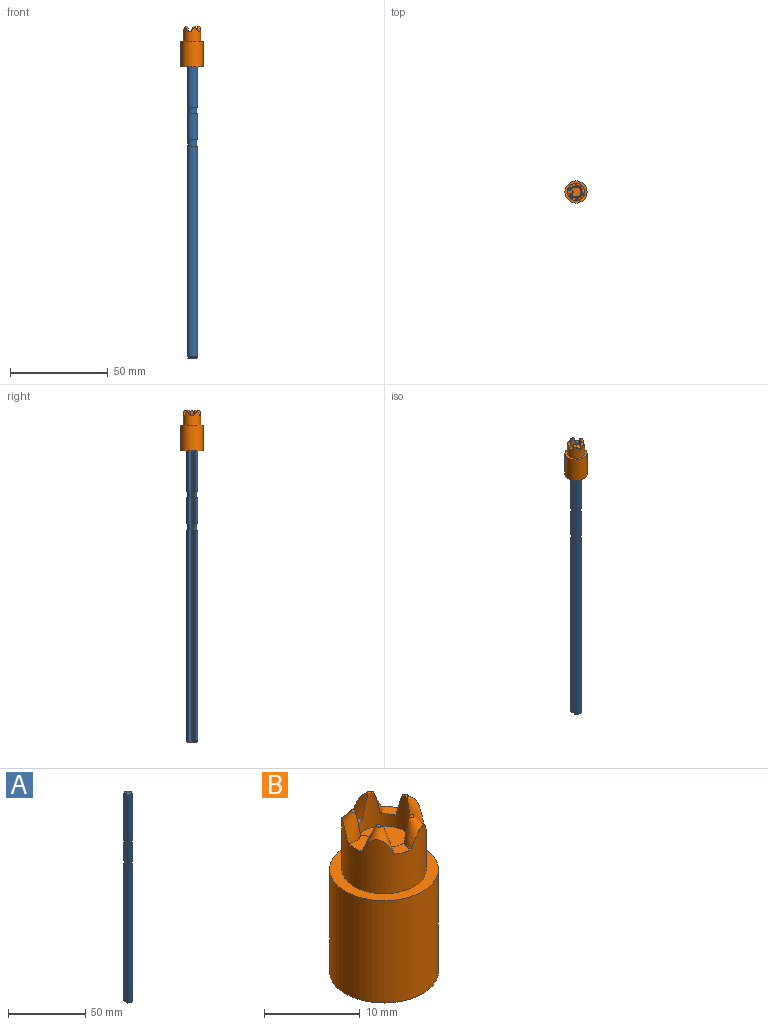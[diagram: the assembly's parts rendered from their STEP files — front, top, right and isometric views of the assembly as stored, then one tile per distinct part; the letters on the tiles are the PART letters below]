
ASSEMBLY  parts=2 mates=1
PART A: 16 faces, bbox 5.6x5.9x165 mm
  f0: cylinder r=2.95mm len=13.2mm, axis (0,0,-1), area 201.2mm2, adj f2,f4,f11,f15
  f1: cylinder r=2.95mm len=107.85mm, axis (0,0,-1), area 1643.7mm2, adj f2,f4,f8,f12
  f2: plane 165.02x1.36mm, normal (-0.71,0.71,0), area 307.8mm2, adj f0,f1,f3,f5,f6,f7,f8,f9
  f3: cylinder r=2.95mm len=35.25mm, axis (0,0,-1), area 537.2mm2, adj f2,f4,f9,f14
  f4: plane 165.02x1.36mm, normal (-0.71,-0.71,0), area 307.8mm2, adj f0,f1,f3,f5,f6,f7,f8,f9
  f5: cylinder r=0.3mm len=165mm, axis (0,0,-1), area 77.8mm2, adj f2,f4,f6,f7
  f6: plane 5.09x4.75mm, normal (0,0,1), area 18.2mm2, adj f2,f4,f5,f9
  f7: plane 4.69x4.41mm, normal (0,0,-1), area 15.6mm2, adj f2,f4,f5,f8
  f8: cone r=2.95mm half-angle=45deg, axis (0,0,1), area 11.7mm2, adj f1,f2,f4,f7
  f9: cone r=2.54mm half-angle=15deg, axis (0,0,-1), area 22.2mm2, adj f2,f3,f4,f6
  f10: cylinder r=2.4mm len=4.8mm, axis (0,0,-1), area 41.8mm2, adj f2,f4,f11,f12
  f11: plane 5.89x5.45mm, normal (0,0,-1), area 7.6mm2, adj f0,f2,f4,f10
  f12: plane 5.89x5.45mm, normal (0,0,1), area 7.6mm2, adj f1,f2,f4,f10
  f13: cylinder r=2.4mm len=4.8mm, axis (0,0,-1), area 41.8mm2, adj f2,f4,f14,f15
  f14: plane 5.89x5.45mm, normal (0,0,-1), area 7.6mm2, adj f2,f3,f4,f13
  f15: plane 5.89x5.45mm, normal (0,0,1), area 7.6mm2, adj f0,f2,f4,f13
PART B: 33 faces, bbox 11.7x11.7x21.3 mm
  f0: cylinder r=3.06mm len=6.12mm, axis (0,0,-1), area 44.5mm2, adj f1,f4,f6,f7,f10,f11,f12,f13
  f1: cylinder r=0.15mm len=4.37mm, axis (0,0,-1), area 0.8mm2, adj f0,f2,f17,f32
  f2: plane 3.77x0.68mm, normal (0.71,0.71,0), area 1.9mm2, adj f1,f5,f17,f18,f32
  f3: plane 3.77x0.68mm, normal (0.71,-0.71,0), area 1.9mm2, adj f4,f5,f18,f22,f32
  f4: cylinder r=0.15mm len=4.37mm, axis (0,0,-1), area 0.8mm2, adj f0,f3,f22,f32
  f5: cylinder r=0.9mm len=1.57mm, axis (0,0,-1), area 2.2mm2, adj f2,f3,f18,f32
  f6: cone r=1.8mm half-angle=24.8deg, axis (0.34,0,-0.94), area 9mm2, adj f0,f7,f9,f10,f27
  f7: plane 0.97x0.71mm, normal (0,0,1), area 0.2mm2, adj f0,f6
  f8: cylinder r=3.06mm len=15.9mm, axis (0,0,-1), area 255.9mm2, adj f15,f21,f29,f31
  f9: cylinder r=4.4mm len=8.8mm, axis (0,0,-1), area 159.2mm2, adj f6,f10,f12,f13,f17,f18,f22,f23
  f10: plane 2.32x2.22mm, normal (0,0,1), area 2.2mm2, adj f0,f6,f9,f12
  f11: plane 0.97x0.81mm, normal (0,0,1), area 0.2mm2, adj f0,f12
  f12: cone r=1.8mm half-angle=24.8deg, axis (0.11,0.33,-0.94), area 9mm2, adj f0,f9,f10,f11,f13
  f13: plane 2.2x1.91mm, normal (0,0,1), area 2.2mm2, adj f0,f9,f12,f17
  f14: plane 0.63x0.58mm, normal (0,0,1), area 0.2mm2, adj f0,f17
  f15: cylinder r=0.15mm len=15.9mm, axis (0,0,-1), area 3.1mm2, adj f8,f16,f29,f31
  f16: plane 15.9x0.68mm, normal (0.71,0.71,0), area 15.3mm2, adj f15,f26,f29,f31
  f17: cone r=1.8mm half-angle=24.8deg, axis (-0.28,0.2,-0.94), area 9.8mm2, adj f0,f1,f2,f9,f13,f14,f18
  f18: plane 2.7x2.17mm, normal (0,0,1), area 4.4mm2, adj f2,f3,f5,f9,f17,f22
  f19: plane 0.63x0.58mm, normal (0,0,1), area 0.2mm2, adj f0,f22
  f20: plane 15.9x0.68mm, normal (0.71,-0.71,0), area 15.3mm2, adj f21,f26,f29,f31
  f21: cylinder r=0.15mm len=15.9mm, axis (0,0,-1), area 3.1mm2, adj f8,f20,f29,f31
  f22: cone r=1.8mm half-angle=24.8deg, axis (-0.28,-0.2,-0.94), area 9.8mm2, adj f0,f3,f4,f9,f18,f19,f23
  f23: plane 2.2x1.91mm, normal (0,0,1), area 2.2mm2, adj f0,f9,f22,f24
  f24: cone r=1.8mm half-angle=24.8deg, axis (0.11,-0.33,-0.94), area 9mm2, adj f0,f9,f23,f25,f27
  f25: plane 0.97x0.81mm, normal (0,0,1), area 0.2mm2, adj f0,f24
  f26: cylinder r=0.9mm len=15.9mm, axis (0,0,-1), area 22.5mm2, adj f16,f20,f29,f31
  f27: plane 2.32x2.22mm, normal (0,0,1), area 2.2mm2, adj f0,f6,f9,f24
  f28: cylinder r=5.68mm len=13.05mm, axis (0,0,1), area 465.3mm2, adj f29,f30
  f29: plane 11.35x11.35mm, normal (0,0,-1), area 74.2mm2, adj f8,f15,f16,f20,f21,f26,f28
  f30: plane 11.35x11.35mm, normal (0,0,1), area 40.4mm2, adj f9,f28
  f31: plane 6.12x5.75mm, normal (0,0,-1), area 27mm2, adj f8,f15,f16,f20,f21,f26
  f32: plane 6.12x5.75mm, normal (0,0,1), area 27mm2, adj f0,f1,f2,f3,f4,f5
PLACE A t=(0,0,-162.15)mm
PLACE B at identity fixed
MATE fastened A.f0 <-> B.f0  axis (0,0,1) through (0,0,2.85)mm
